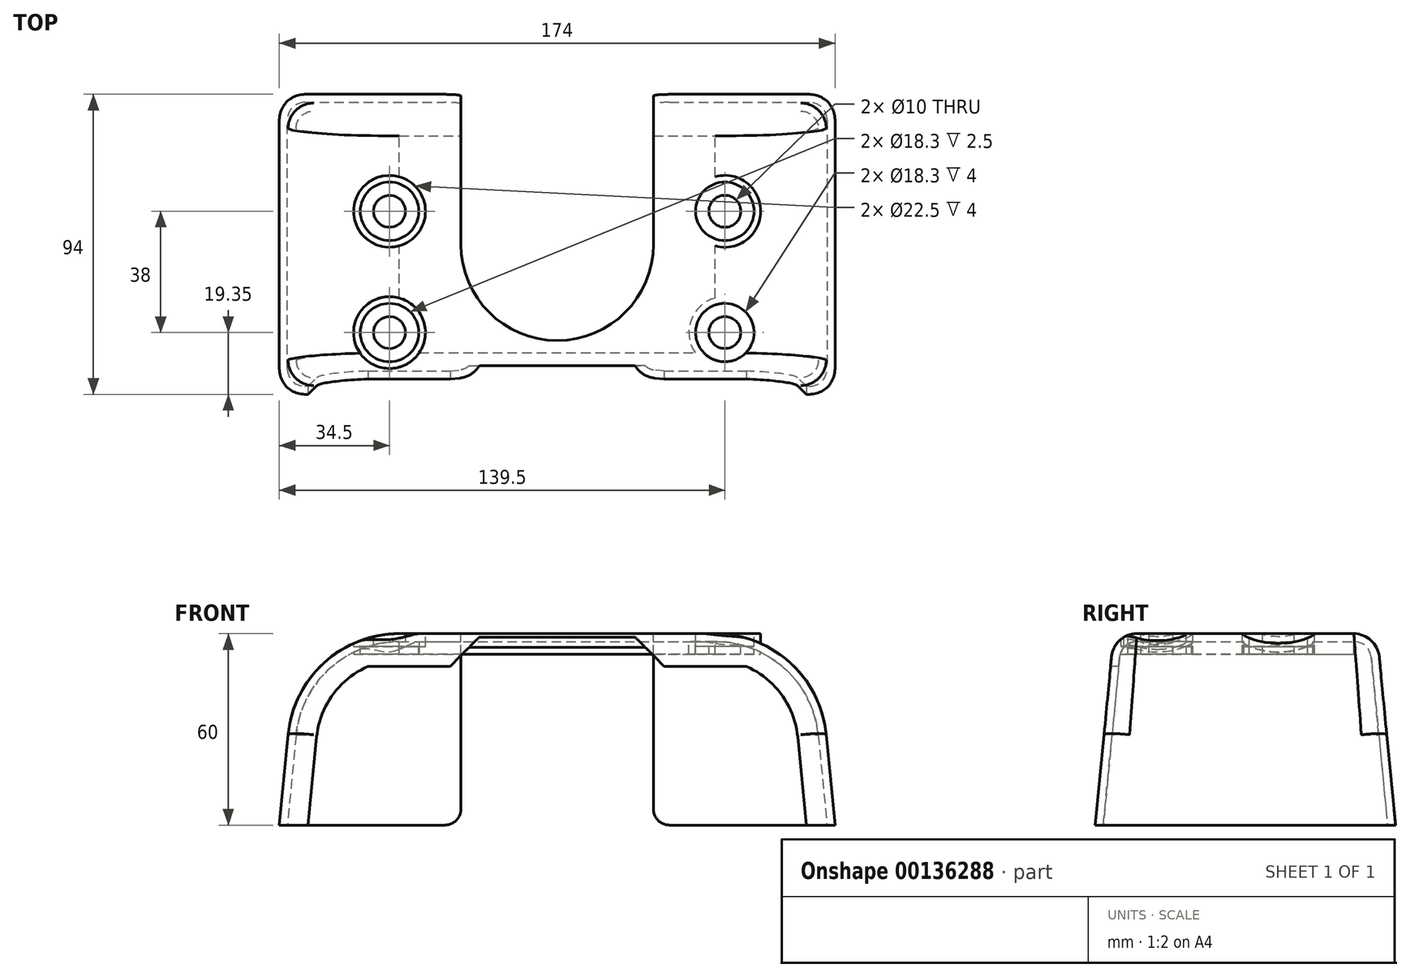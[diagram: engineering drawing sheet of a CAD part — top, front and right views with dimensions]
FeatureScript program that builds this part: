
annotation { "Feature Type Name" : "Feature", "Feature Type Description" : "" }
export const myFeature = defineFeature(function(context is Context, id is Id, definition is map)
    precondition{}
    {
        {
            var Q0;
            Q0=qCreatedBy(makeId("Top.planeOp"),FACE);
            var sketch = newSketch(context, id + "F0", { "sketchPlane" : qUnion([Q0])});
            skLineSegment(sketch, "E0.bottom", {"start": v(-87, -47) * mm, "end": v(87, -47) * mm});
            skLineSegment(sketch, "E0.top", {"start": v(-87, 47) * mm, "end": v(87, 47) * mm});
            skLineSegment(sketch, "E0.left", {"start": v(-87, -47) * mm, "end": v(-87, 47) * mm});
            skLineSegment(sketch, "E0.right", {"start": v(87, -47) * mm, "end": v(87, 47) * mm});
            skPoint(sketch, "E0.middle", {"position": v(0, 0) * mm});
            skSolve(sketch);
        }
        {
            var Q0;
            Q0 = qSketchRegion(id + "F0", true);
            extrude(context, id + "F1", {"entities" : qUnion([Q0]), "depth" : 60 * mm, "hasDraft" : true, "draftAngle" : 5.5 * degree, "draftPullDirection" : true});
        }
        {
            var Q0;
            Q0=makeQuery(id+"F1.opExtrude","CAP_EDGE",EDGE,{"disambiguationData":[OSD([sQuery(id+"F0.wireOp",EDGE,"E0.left")])],"isStart":false});
            var Q1;
            Q1=makeQuery(id+"F1.opExtrude","CAP_EDGE",EDGE,{"disambiguationData":[OSD([sQuery(id+"F0.wireOp",EDGE,"E0.right")])],"isStart":false});
            fillet(context, id + "F2", {"entities" : qUnion([Q0, Q1]), "radius" : 35 * mm, "tangentPropagation" : true, "allowEdgeOverflow" : false});
        }
        {
            var Q0;
            Q0=makeQuery(id+"F1.opExtrude","SWEPT_EDGE",EDGE,{"disambiguationData":[OSD([sQuery(id+"F0.wireOp",EDGE,"E0.bottom"),sQuery(id+"F0.wireOp",EDGE,"E0.left")])]});
            var Q1;
            Q1=makeQuery(id+"F2.opFillet","BLEND_EDGE",EDGE,{"blendedFrom":[makeQuery(id+"F1.opExtrude","CAP_EDGE",EDGE,{"disambiguationData":[OSD([sQuery(id+"F0.wireOp",EDGE,"E0.left")])],"isStart":false}),makeQuery(id+"F1.opExtrude","SWEPT_FACE",FACE,{"disambiguationData":[OSD([sQuery(id+"F0.wireOp",EDGE,"E0.bottom")])]})],"blendedInto":[makeQuery(id+"F1.opExtrude","SWEPT_FACE",FACE,{"disambiguationData":[OSD([sQuery(id+"F0.wireOp",EDGE,"E0.bottom")])]})]});
            var Q2;
            Q2=makeQuery(id+"F1.opExtrude","SWEPT_EDGE",EDGE,{"disambiguationData":[OSD([sQuery(id+"F0.wireOp",EDGE,"E0.top"),sQuery(id+"F0.wireOp",EDGE,"E0.left")])]});
            fillet(context, id + "F3", {"entities" : qUnion([Q0, Q1, Q2]), "radius" : 8 * mm, "tangentPropagation" : true, "allowEdgeOverflow" : false});
        }
        {
            var Q0;
            Q0=makeQuery(id+"F1.opExtrude","CAP_FACE",FACE,{"disambiguationData":[OSD([sQuery(id+"F0.wireOp",EDGE,"E0.bottom"),sQuery(id+"F0.wireOp",EDGE,"E0.top"),sQuery(id+"F0.wireOp",EDGE,"E0.left"),sQuery(id+"F0.wireOp",EDGE,"E0.right")])],"isStart":true});
            shell(context, id + "F4", {"entities" : qUnion([Q0]), "thickness" : 2.5 * mm});
        }
        {
            var Q0;
            Q0=makeQuery(id+"F1.opExtrude","SWEPT_FACE",FACE,{"disambiguationData":[OSD([sQuery(id+"F0.wireOp",EDGE,"E0.bottom")])]});
            var sketch = newSketch(context, id + "F5", { "sketchPlane" : qUnion([Q0])});
            skLineSegment(sketch, "E1", {"start": v(-79.04, -4.5) * mm, "end": v(-73.96, 48.5) * mm});
            skLineSegment(sketch, "E2", {"start": v(79.04, -4.5) * mm, "end": v(73.96, 48.5) * mm});
            skPoint(sketch, "E3.orphan", {"position": v(76.3, 48.5) * mm});
            skLineSegment(sketch, "E4", {"start": v(0, -4.5) * mm, "end": v(0, 43) * mm, "construction": true});
            skPoint(sketch, "E4.endSnap0", {"position": v(0, 48.5) * mm});
            skSolve(sketch);
        }
        {
            var Q0;
            Q0=makeQuery(id+"F1.opExtrude","CAP_FACE",FACE,{"disambiguationData":[OSD([sQuery(id+"F0.wireOp",EDGE,"E0.bottom"),sQuery(id+"F0.wireOp",EDGE,"E0.top"),sQuery(id+"F0.wireOp",EDGE,"E0.left"),sQuery(id+"F0.wireOp",EDGE,"E0.right")])],"isStart":false});
            var sketch = newSketch(context, id + "F6", { "sketchPlane" : qUnion([Q0])});
            skArc(sketch, "E5", {"start": v(-30.15, 0) * mm, "mid": v(0, -30.15) * mm, "end": v(30.15, 0) * mm});
            skLineSegment(sketch, "E6.top", {"start": v(-30.15, 60.3) * mm, "end": v(30.15, 60.3) * mm});
            skLineSegment(sketch, "E6.left", {"start": v(-30.15, 0) * mm, "end": v(-30.15, 60.3) * mm});
            skLineSegment(sketch, "E6.right", {"start": v(30.15, 0) * mm, "end": v(30.15, 60.3) * mm});
            skCircle(sketch, "E7", {"center": v(-52.5, -27.65) * mm, "radius": 11.25 * mm});
            skCircle(sketch, "E8.MirrorC", {"center": v(52.5, -27.65) * mm, "radius": 11.25 * mm});
            skCircle(sketch, "E9.MirrorC", {"center": v(-52.5, 10.35) * mm, "radius": 11.25 * mm});
            skLineSegment(sketch, "E10", {"start": v(-52.3, -38.9) * mm, "end": v(52.5, -38.9) * mm, "construction": true});
            skLineSegment(sketch, "E11", {"start": v(-52.5, -27.65) * mm, "end": v(52.5, -27.65) * mm, "construction": true});
            skPoint(sketch, "E12", {"position": v(0, -30.15) * mm});
            skLineSegment(sketch, "E13", {"start": v(-52.5, 10.35) * mm, "end": v(52.5, 10.35) * mm, "construction": true});
            skCircle(sketch, "E14.MirrorC", {"center": v(52.5, 10.35) * mm, "radius": 11.25 * mm});
            skCircle(sketch, "E15", {"center": v(52.5, -27.65) * mm, "radius": 9.15 * mm});
            skCircle(sketch, "E16.MirrorC", {"center": v(-52.5, -27.65) * mm, "radius": 9.15 * mm});
            skCircle(sketch, "E17", {"center": v(52.5, 10.35) * mm, "radius": 9.15 * mm});
            skCircle(sketch, "E18.MirrorC", {"center": v(-52.5, 10.35) * mm, "radius": 9.15 * mm});
            skCircle(sketch, "E19", {"center": v(52.5, -27.65) * mm, "radius": 5 * mm});
            skCircle(sketch, "E20", {"center": v(52.5, 10.35) * mm, "radius": 5 * mm});
            skCircle(sketch, "E21.MirrorC", {"center": v(-52.5, -27.65) * mm, "radius": 5 * mm});
            skCircle(sketch, "E22.MirrorC", {"center": v(-52.5, 10.35) * mm, "radius": 5 * mm});
            skSolve(sketch);
        }
        {
            var Q0;
            {var subQ0=sQuery(id+"F6.wireOp",EDGE,"E6.top");Q0=makeQuery(id+"F6.imprint","IMPRINT",FACE,{"disambiguationData":[TD([[makeQuery(id+"F6.imprint","IMPRINT",EDGE,{"derivedFrom":subQ0}),-1.0]])]});}
            var Q1;
            {var subQ0=sQuery(id+"F6.wireOp",EDGE,"E5");Q1=makeQuery(id+"F6.imprint","IMPRINT",FACE,{"disambiguationData":[TD([[makeQuery(id+"F6.imprint","IMPRINT",EDGE,{"derivedFrom":subQ0}),1.0]])]});}
            extrude(context, id + "F7", {"entities" : qUnion([Q0, Q1]), "operationType" : NewBodyOperationType.REMOVE, "endBound" : BoundingType.THROUGH_ALL, "oppositeDirection" : true, "depth" : 25 * mm});
        }
        {
            var Q0;
            Q0=makeQuery(id+"F7.boolean.opBoolean","INTERSECT",EDGE,{"derivedFrom":[makeQuery(id+"F1.opExtrude","CAP_FACE",FACE,{"disambiguationData":[OSD([sQuery(id+"F0.wireOp",EDGE,"E0.bottom"),sQuery(id+"F0.wireOp",EDGE,"E0.top"),sQuery(id+"F0.wireOp",EDGE,"E0.left"),sQuery(id+"F0.wireOp",EDGE,"E0.right")])],"isStart":true}),makeQuery(id+"F7.opExtrude","SWEPT_FACE",FACE,{"disambiguationData":[OSD([sQuery(id+"F6.wireOp",EDGE,"E6.left")])]})]});
            var Q1;
            Q1=makeQuery(id+"F7.boolean.opBoolean","INTERSECT",EDGE,{"derivedFrom":[makeQuery(id+"F1.opExtrude","CAP_FACE",FACE,{"disambiguationData":[OSD([sQuery(id+"F0.wireOp",EDGE,"E0.bottom"),sQuery(id+"F0.wireOp",EDGE,"E0.top"),sQuery(id+"F0.wireOp",EDGE,"E0.left"),sQuery(id+"F0.wireOp",EDGE,"E0.right")])],"isStart":true}),makeQuery(id+"F7.opExtrude","SWEPT_FACE",FACE,{"disambiguationData":[OSD([sQuery(id+"F6.wireOp",EDGE,"E6.right")])]})]});
            fillet(context, id + "F8", {"entities" : qUnion([Q0, Q1]), "radius" : 5 * mm, "tangentPropagation" : true, "allowEdgeOverflow" : false});
        }
        {
            var Q0;
            {var subQ0=sQuery(id+"F6.wireOp",EDGE,"E16.MirrorC");var subQ1=sQuery(id+"F0.wireOp",EDGE,"E0.left");var subQ2=sQuery(id+"F0.wireOp",EDGE,"E0.bottom");var subQ3=makeQuery(id+"F1.opExtrude","CAP_FACE",FACE,{"disambiguationData":[OSD([subQ2,sQuery(id+"F0.wireOp",EDGE,"E0.top"),subQ1,sQuery(id+"F0.wireOp",EDGE,"E0.right")])],"isStart":false});var subQ4=makeQuery(id+"F3.opFillet","BLEND_EDGE",EDGE,{"blendedFrom":[makeQuery(id+"F1.opExtrude","CAP_EDGE",EDGE,{"disambiguationData":[OSD([subQ2])],"isStart":false}),subQ3],"blendedInto":[subQ3]});var subQ5=makeQuery(id+"F6.imprint","INTERSECT",VERTEX,{"derivedFrom":[subQ4,subQ0]});Q0=makeQuery(id+"F6.imprint","IMPRINT",FACE,{"disambiguationData":[TD([[makeQuery(id+"F6.imprint","IMPRINT",EDGE,{"disambiguationData":[TD([[subQ5,-1.0]])],"derivedFrom":subQ0}),-1.0]])]});}
            var Q1;
            {var subQ0=sQuery(id+"F6.wireOp",EDGE,"E7");var subQ1=sQuery(id+"F0.wireOp",EDGE,"E0.left");var subQ2=sQuery(id+"F0.wireOp",EDGE,"E0.bottom");var subQ3=makeQuery(id+"F1.opExtrude","CAP_FACE",FACE,{"disambiguationData":[OSD([subQ2,sQuery(id+"F0.wireOp",EDGE,"E0.top"),subQ1,sQuery(id+"F0.wireOp",EDGE,"E0.right")])],"isStart":false});var subQ4=makeQuery(id+"F3.opFillet","BLEND_EDGE",EDGE,{"blendedFrom":[makeQuery(id+"F1.opExtrude","CAP_EDGE",EDGE,{"disambiguationData":[OSD([subQ2])],"isStart":false}),subQ3],"blendedInto":[subQ3]});var subQ5=makeQuery(id+"F6.imprint","INTERSECT",VERTEX,{"derivedFrom":[subQ4,subQ0]});Q1=makeQuery(id+"F6.imprint","IMPRINT",FACE,{"disambiguationData":[TD([[makeQuery(id+"F6.imprint","IMPRINT",EDGE,{"disambiguationData":[TD([[subQ5,1.0]])],"derivedFrom":subQ0}),1.0]])]});}
            var Q2;
            {var subQ0=sQuery(id+"F6.wireOp",EDGE,"E16.MirrorC");var subQ1=sQuery(id+"F0.wireOp",EDGE,"E0.left");var subQ2=sQuery(id+"F0.wireOp",EDGE,"E0.bottom");var subQ3=makeQuery(id+"F1.opExtrude","CAP_FACE",FACE,{"disambiguationData":[OSD([subQ2,sQuery(id+"F0.wireOp",EDGE,"E0.top"),subQ1,sQuery(id+"F0.wireOp",EDGE,"E0.right")])],"isStart":false});var subQ4=makeQuery(id+"F3.opFillet","BLEND_EDGE",EDGE,{"blendedFrom":[makeQuery(id+"F1.opExtrude","CAP_EDGE",EDGE,{"disambiguationData":[OSD([subQ2])],"isStart":false}),subQ3],"blendedInto":[subQ3]});var subQ5=makeQuery(id+"F6.imprint","INTERSECT",VERTEX,{"derivedFrom":[subQ4,subQ0]});Q2=makeQuery(id+"F6.imprint","IMPRINT",FACE,{"disambiguationData":[TD([[makeQuery(id+"F6.imprint","IMPRINT",EDGE,{"disambiguationData":[TD([[subQ5,1.0]])],"derivedFrom":subQ0}),-1.0]])]});}
            var Q3;
            {var subQ0=sQuery(id+"F6.wireOp",EDGE,"E7");var subQ1=sQuery(id+"F0.wireOp",EDGE,"E0.left");var subQ2=sQuery(id+"F0.wireOp",EDGE,"E0.bottom");var subQ3=makeQuery(id+"F1.opExtrude","CAP_FACE",FACE,{"disambiguationData":[OSD([subQ2,sQuery(id+"F0.wireOp",EDGE,"E0.top"),subQ1,sQuery(id+"F0.wireOp",EDGE,"E0.right")])],"isStart":false});var subQ4=makeQuery(id+"F3.opFillet","BLEND_EDGE",EDGE,{"blendedFrom":[makeQuery(id+"F1.opExtrude","CAP_EDGE",EDGE,{"disambiguationData":[OSD([subQ2])],"isStart":false}),subQ3],"blendedInto":[subQ3]});var subQ5=makeQuery(id+"F6.imprint","INTERSECT",VERTEX,{"derivedFrom":[subQ4,subQ0]});Q3=makeQuery(id+"F6.imprint","IMPRINT",FACE,{"disambiguationData":[TD([[makeQuery(id+"F6.imprint","IMPRINT",EDGE,{"disambiguationData":[TD([[subQ5,-1.0]])],"derivedFrom":subQ0}),1.0]])]});}
            var Q4;
            {var subQ0=sQuery(id+"F6.wireOp",EDGE,"E9.MirrorC");var subQ1=sQuery(id+"F0.wireOp",EDGE,"E0.left");var subQ2=makeQuery(id+"F2.opFillet","BLEND_EDGE",EDGE,{"blendedFrom":[makeQuery(id+"F1.opExtrude","CAP_EDGE",EDGE,{"disambiguationData":[OSD([subQ1])],"isStart":false}),makeQuery(id+"F1.opExtrude","CAP_FACE",FACE,{"disambiguationData":[OSD([sQuery(id+"F0.wireOp",EDGE,"E0.bottom"),sQuery(id+"F0.wireOp",EDGE,"E0.top"),subQ1,sQuery(id+"F0.wireOp",EDGE,"E0.right")])],"isStart":false})],"blendedInto":[makeQuery(id+"F1.opExtrude","CAP_FACE",FACE,{"disambiguationData":[OSD([sQuery(id+"F0.wireOp",EDGE,"E0.bottom"),sQuery(id+"F0.wireOp",EDGE,"E0.top"),subQ1,sQuery(id+"F0.wireOp",EDGE,"E0.right")])],"isStart":false})]});var subQ3=makeQuery(id+"F6.imprint","INTERSECT",VERTEX,{"disambiguationData":[OD(0.0)],"derivedFrom":[subQ2,subQ0]});Q4=makeQuery(id+"F6.imprint","IMPRINT",FACE,{"disambiguationData":[TD([[makeQuery(id+"F6.imprint","IMPRINT",EDGE,{"disambiguationData":[TD([[subQ3,1.0]])],"derivedFrom":subQ0}),-1.0]])]});}
            var Q5;
            {var subQ0=sQuery(id+"F6.wireOp",EDGE,"E18.MirrorC");var subQ1=sQuery(id+"F0.wireOp",EDGE,"E0.left");var subQ2=makeQuery(id+"F2.opFillet","BLEND_EDGE",EDGE,{"blendedFrom":[makeQuery(id+"F1.opExtrude","CAP_EDGE",EDGE,{"disambiguationData":[OSD([subQ1])],"isStart":false}),makeQuery(id+"F1.opExtrude","CAP_FACE",FACE,{"disambiguationData":[OSD([sQuery(id+"F0.wireOp",EDGE,"E0.bottom"),sQuery(id+"F0.wireOp",EDGE,"E0.top"),subQ1,sQuery(id+"F0.wireOp",EDGE,"E0.right")])],"isStart":false})],"blendedInto":[makeQuery(id+"F1.opExtrude","CAP_FACE",FACE,{"disambiguationData":[OSD([sQuery(id+"F0.wireOp",EDGE,"E0.bottom"),sQuery(id+"F0.wireOp",EDGE,"E0.top"),subQ1,sQuery(id+"F0.wireOp",EDGE,"E0.right")])],"isStart":false})]});var subQ3=makeQuery(id+"F6.imprint","INTERSECT",VERTEX,{"disambiguationData":[OD(0.0)],"derivedFrom":[subQ2,subQ0]});Q5=makeQuery(id+"F6.imprint","IMPRINT",FACE,{"disambiguationData":[TD([[makeQuery(id+"F6.imprint","IMPRINT",EDGE,{"disambiguationData":[TD([[subQ3,1.0]])],"derivedFrom":subQ0}),-1.0]])]});}
            var Q6;
            {var subQ0=sQuery(id+"F6.wireOp",EDGE,"E9.MirrorC");var subQ1=sQuery(id+"F0.wireOp",EDGE,"E0.left");var subQ2=makeQuery(id+"F2.opFillet","BLEND_EDGE",EDGE,{"blendedFrom":[makeQuery(id+"F1.opExtrude","CAP_EDGE",EDGE,{"disambiguationData":[OSD([subQ1])],"isStart":false}),makeQuery(id+"F1.opExtrude","CAP_FACE",FACE,{"disambiguationData":[OSD([sQuery(id+"F0.wireOp",EDGE,"E0.bottom"),sQuery(id+"F0.wireOp",EDGE,"E0.top"),subQ1,sQuery(id+"F0.wireOp",EDGE,"E0.right")])],"isStart":false})],"blendedInto":[makeQuery(id+"F1.opExtrude","CAP_FACE",FACE,{"disambiguationData":[OSD([sQuery(id+"F0.wireOp",EDGE,"E0.bottom"),sQuery(id+"F0.wireOp",EDGE,"E0.top"),subQ1,sQuery(id+"F0.wireOp",EDGE,"E0.right")])],"isStart":false})]});var subQ3=makeQuery(id+"F6.imprint","INTERSECT",VERTEX,{"disambiguationData":[OD(0.0)],"derivedFrom":[subQ2,subQ0]});Q6=makeQuery(id+"F6.imprint","IMPRINT",FACE,{"disambiguationData":[TD([[makeQuery(id+"F6.imprint","IMPRINT",EDGE,{"disambiguationData":[TD([[subQ3,-1.0]])],"derivedFrom":subQ0}),-1.0]])]});}
            var Q7;
            {var subQ0=sQuery(id+"F6.wireOp",EDGE,"E18.MirrorC");var subQ1=sQuery(id+"F0.wireOp",EDGE,"E0.left");var subQ2=makeQuery(id+"F2.opFillet","BLEND_EDGE",EDGE,{"blendedFrom":[makeQuery(id+"F1.opExtrude","CAP_EDGE",EDGE,{"disambiguationData":[OSD([subQ1])],"isStart":false}),makeQuery(id+"F1.opExtrude","CAP_FACE",FACE,{"disambiguationData":[OSD([sQuery(id+"F0.wireOp",EDGE,"E0.bottom"),sQuery(id+"F0.wireOp",EDGE,"E0.top"),subQ1,sQuery(id+"F0.wireOp",EDGE,"E0.right")])],"isStart":false})],"blendedInto":[makeQuery(id+"F1.opExtrude","CAP_FACE",FACE,{"disambiguationData":[OSD([sQuery(id+"F0.wireOp",EDGE,"E0.bottom"),sQuery(id+"F0.wireOp",EDGE,"E0.top"),subQ1,sQuery(id+"F0.wireOp",EDGE,"E0.right")])],"isStart":false})]});var subQ3=makeQuery(id+"F6.imprint","INTERSECT",VERTEX,{"disambiguationData":[OD(0.0)],"derivedFrom":[subQ2,subQ0]});Q7=makeQuery(id+"F6.imprint","IMPRINT",FACE,{"disambiguationData":[TD([[makeQuery(id+"F6.imprint","IMPRINT",EDGE,{"disambiguationData":[TD([[subQ3,-1.0]])],"derivedFrom":subQ0}),-1.0]])]});}
            var Q8;
            {var subQ0=sQuery(id+"F6.wireOp",EDGE,"E15");var subQ1=sQuery(id+"F0.wireOp",EDGE,"E0.right");var subQ2=sQuery(id+"F0.wireOp",EDGE,"E0.bottom");var subQ3=makeQuery(id+"F1.opExtrude","CAP_FACE",FACE,{"disambiguationData":[OSD([subQ2,sQuery(id+"F0.wireOp",EDGE,"E0.top"),sQuery(id+"F0.wireOp",EDGE,"E0.left"),subQ1])],"isStart":false});var subQ4=makeQuery(id+"F3.opFillet","BLEND_EDGE",EDGE,{"blendedFrom":[makeQuery(id+"F1.opExtrude","CAP_EDGE",EDGE,{"disambiguationData":[OSD([subQ2])],"isStart":false}),subQ3],"blendedInto":[subQ3]});var subQ5=makeQuery(id+"F6.imprint","INTERSECT",VERTEX,{"derivedFrom":[subQ4,subQ0]});Q8=makeQuery(id+"F6.imprint","IMPRINT",FACE,{"disambiguationData":[TD([[makeQuery(id+"F6.imprint","IMPRINT",EDGE,{"disambiguationData":[TD([[subQ5,-1.0]])],"derivedFrom":subQ0}),1.0]])]});}
            var Q9;
            {var subQ0=sQuery(id+"F6.wireOp",EDGE,"E8.MirrorC");var subQ1=sQuery(id+"F0.wireOp",EDGE,"E0.right");var subQ2=sQuery(id+"F0.wireOp",EDGE,"E0.bottom");var subQ3=makeQuery(id+"F1.opExtrude","CAP_FACE",FACE,{"disambiguationData":[OSD([subQ2,sQuery(id+"F0.wireOp",EDGE,"E0.top"),sQuery(id+"F0.wireOp",EDGE,"E0.left"),subQ1])],"isStart":false});var subQ4=makeQuery(id+"F3.opFillet","BLEND_EDGE",EDGE,{"blendedFrom":[makeQuery(id+"F1.opExtrude","CAP_EDGE",EDGE,{"disambiguationData":[OSD([subQ2])],"isStart":false}),subQ3],"blendedInto":[subQ3]});var subQ5=makeQuery(id+"F6.imprint","INTERSECT",VERTEX,{"derivedFrom":[subQ4,subQ0]});Q9=makeQuery(id+"F6.imprint","IMPRINT",FACE,{"disambiguationData":[TD([[makeQuery(id+"F6.imprint","IMPRINT",EDGE,{"disambiguationData":[TD([[subQ5,1.0]])],"derivedFrom":subQ0}),-1.0]])]});}
            var Q10;
            {var subQ0=sQuery(id+"F6.wireOp",EDGE,"E15");var subQ1=sQuery(id+"F0.wireOp",EDGE,"E0.right");var subQ2=sQuery(id+"F0.wireOp",EDGE,"E0.bottom");var subQ3=makeQuery(id+"F1.opExtrude","CAP_FACE",FACE,{"disambiguationData":[OSD([subQ2,sQuery(id+"F0.wireOp",EDGE,"E0.top"),sQuery(id+"F0.wireOp",EDGE,"E0.left"),subQ1])],"isStart":false});var subQ4=makeQuery(id+"F3.opFillet","BLEND_EDGE",EDGE,{"blendedFrom":[makeQuery(id+"F1.opExtrude","CAP_EDGE",EDGE,{"disambiguationData":[OSD([subQ2])],"isStart":false}),subQ3],"blendedInto":[subQ3]});var subQ5=makeQuery(id+"F6.imprint","INTERSECT",VERTEX,{"derivedFrom":[subQ4,subQ0]});Q10=makeQuery(id+"F6.imprint","IMPRINT",FACE,{"disambiguationData":[TD([[makeQuery(id+"F6.imprint","IMPRINT",EDGE,{"disambiguationData":[TD([[subQ5,1.0]])],"derivedFrom":subQ0}),1.0]])]});}
            var Q11;
            {var subQ0=sQuery(id+"F6.wireOp",EDGE,"E8.MirrorC");var subQ1=sQuery(id+"F0.wireOp",EDGE,"E0.right");var subQ2=sQuery(id+"F0.wireOp",EDGE,"E0.bottom");var subQ3=makeQuery(id+"F1.opExtrude","CAP_FACE",FACE,{"disambiguationData":[OSD([subQ2,sQuery(id+"F0.wireOp",EDGE,"E0.top"),sQuery(id+"F0.wireOp",EDGE,"E0.left"),subQ1])],"isStart":false});var subQ4=makeQuery(id+"F3.opFillet","BLEND_EDGE",EDGE,{"blendedFrom":[makeQuery(id+"F1.opExtrude","CAP_EDGE",EDGE,{"disambiguationData":[OSD([subQ2])],"isStart":false}),subQ3],"blendedInto":[subQ3]});var subQ5=makeQuery(id+"F6.imprint","INTERSECT",VERTEX,{"derivedFrom":[subQ4,subQ0]});Q11=makeQuery(id+"F6.imprint","IMPRINT",FACE,{"disambiguationData":[TD([[makeQuery(id+"F6.imprint","IMPRINT",EDGE,{"disambiguationData":[TD([[subQ5,-1.0]])],"derivedFrom":subQ0}),-1.0]])]});}
            var Q12;
            {var subQ0=sQuery(id+"F6.wireOp",EDGE,"E14.MirrorC");var subQ1=sQuery(id+"F0.wireOp",EDGE,"E0.right");var subQ2=makeQuery(id+"F2.opFillet","BLEND_EDGE",EDGE,{"blendedFrom":[makeQuery(id+"F1.opExtrude","CAP_EDGE",EDGE,{"disambiguationData":[OSD([subQ1])],"isStart":false}),makeQuery(id+"F1.opExtrude","CAP_FACE",FACE,{"disambiguationData":[OSD([sQuery(id+"F0.wireOp",EDGE,"E0.bottom"),sQuery(id+"F0.wireOp",EDGE,"E0.top"),sQuery(id+"F0.wireOp",EDGE,"E0.left"),subQ1])],"isStart":false})],"blendedInto":[makeQuery(id+"F1.opExtrude","CAP_FACE",FACE,{"disambiguationData":[OSD([sQuery(id+"F0.wireOp",EDGE,"E0.bottom"),sQuery(id+"F0.wireOp",EDGE,"E0.top"),sQuery(id+"F0.wireOp",EDGE,"E0.left"),subQ1])],"isStart":false})]});var subQ3=makeQuery(id+"F6.imprint","INTERSECT",VERTEX,{"disambiguationData":[OD(0.0)],"derivedFrom":[subQ2,subQ0]});Q12=makeQuery(id+"F6.imprint","IMPRINT",FACE,{"disambiguationData":[TD([[makeQuery(id+"F6.imprint","IMPRINT",EDGE,{"disambiguationData":[TD([[subQ3,-1.0]])],"derivedFrom":subQ0}),1.0]])]});}
            var Q13;
            {var subQ0=sQuery(id+"F6.wireOp",EDGE,"E17");var subQ1=sQuery(id+"F0.wireOp",EDGE,"E0.right");var subQ2=makeQuery(id+"F2.opFillet","BLEND_EDGE",EDGE,{"blendedFrom":[makeQuery(id+"F1.opExtrude","CAP_EDGE",EDGE,{"disambiguationData":[OSD([subQ1])],"isStart":false}),makeQuery(id+"F1.opExtrude","CAP_FACE",FACE,{"disambiguationData":[OSD([sQuery(id+"F0.wireOp",EDGE,"E0.bottom"),sQuery(id+"F0.wireOp",EDGE,"E0.top"),sQuery(id+"F0.wireOp",EDGE,"E0.left"),subQ1])],"isStart":false})],"blendedInto":[makeQuery(id+"F1.opExtrude","CAP_FACE",FACE,{"disambiguationData":[OSD([sQuery(id+"F0.wireOp",EDGE,"E0.bottom"),sQuery(id+"F0.wireOp",EDGE,"E0.top"),sQuery(id+"F0.wireOp",EDGE,"E0.left"),subQ1])],"isStart":false})]});var subQ3=makeQuery(id+"F6.imprint","INTERSECT",VERTEX,{"disambiguationData":[OD(0.0)],"derivedFrom":[subQ2,subQ0]});Q13=makeQuery(id+"F6.imprint","IMPRINT",FACE,{"disambiguationData":[TD([[makeQuery(id+"F6.imprint","IMPRINT",EDGE,{"disambiguationData":[TD([[subQ3,-1.0]])],"derivedFrom":subQ0}),1.0]])]});}
            var Q14;
            {var subQ0=sQuery(id+"F6.wireOp",EDGE,"E17");var subQ1=sQuery(id+"F0.wireOp",EDGE,"E0.right");var subQ2=makeQuery(id+"F2.opFillet","BLEND_EDGE",EDGE,{"blendedFrom":[makeQuery(id+"F1.opExtrude","CAP_EDGE",EDGE,{"disambiguationData":[OSD([subQ1])],"isStart":false}),makeQuery(id+"F1.opExtrude","CAP_FACE",FACE,{"disambiguationData":[OSD([sQuery(id+"F0.wireOp",EDGE,"E0.bottom"),sQuery(id+"F0.wireOp",EDGE,"E0.top"),sQuery(id+"F0.wireOp",EDGE,"E0.left"),subQ1])],"isStart":false})],"blendedInto":[makeQuery(id+"F1.opExtrude","CAP_FACE",FACE,{"disambiguationData":[OSD([sQuery(id+"F0.wireOp",EDGE,"E0.bottom"),sQuery(id+"F0.wireOp",EDGE,"E0.top"),sQuery(id+"F0.wireOp",EDGE,"E0.left"),subQ1])],"isStart":false})]});var subQ3=makeQuery(id+"F6.imprint","INTERSECT",VERTEX,{"disambiguationData":[OD(0.0)],"derivedFrom":[subQ2,subQ0]});Q14=makeQuery(id+"F6.imprint","IMPRINT",FACE,{"disambiguationData":[TD([[makeQuery(id+"F6.imprint","IMPRINT",EDGE,{"disambiguationData":[TD([[subQ3,1.0]])],"derivedFrom":subQ0}),1.0]])]});}
            var Q15;
            {var subQ0=sQuery(id+"F6.wireOp",EDGE,"E14.MirrorC");var subQ1=sQuery(id+"F0.wireOp",EDGE,"E0.right");var subQ2=makeQuery(id+"F2.opFillet","BLEND_EDGE",EDGE,{"blendedFrom":[makeQuery(id+"F1.opExtrude","CAP_EDGE",EDGE,{"disambiguationData":[OSD([subQ1])],"isStart":false}),makeQuery(id+"F1.opExtrude","CAP_FACE",FACE,{"disambiguationData":[OSD([sQuery(id+"F0.wireOp",EDGE,"E0.bottom"),sQuery(id+"F0.wireOp",EDGE,"E0.top"),sQuery(id+"F0.wireOp",EDGE,"E0.left"),subQ1])],"isStart":false})],"blendedInto":[makeQuery(id+"F1.opExtrude","CAP_FACE",FACE,{"disambiguationData":[OSD([sQuery(id+"F0.wireOp",EDGE,"E0.bottom"),sQuery(id+"F0.wireOp",EDGE,"E0.top"),sQuery(id+"F0.wireOp",EDGE,"E0.left"),subQ1])],"isStart":false})]});var subQ3=makeQuery(id+"F6.imprint","INTERSECT",VERTEX,{"disambiguationData":[OD(0.0)],"derivedFrom":[subQ2,subQ0]});Q15=makeQuery(id+"F6.imprint","IMPRINT",FACE,{"disambiguationData":[TD([[makeQuery(id+"F6.imprint","IMPRINT",EDGE,{"disambiguationData":[TD([[subQ3,1.0]])],"derivedFrom":subQ0}),1.0]])]});}
            extrude(context, id + "F9", {"entities" : qUnion([Q0, Q1, Q2, Q3, Q4, Q5, Q6, Q7, Q8, Q9, Q10, Q11, Q12, Q13, Q14, Q15]), "operationType" : NewBodyOperationType.ADD, "oppositeDirection" : true, "depth" : 6.5 * mm});
        }
        {
            var Q0;
            {var subQ0=sQuery(id+"F6.wireOp",EDGE,"E15");var subQ1=sQuery(id+"F0.wireOp",EDGE,"E0.right");var subQ2=sQuery(id+"F0.wireOp",EDGE,"E0.bottom");var subQ3=makeQuery(id+"F1.opExtrude","CAP_FACE",FACE,{"disambiguationData":[OSD([subQ2,sQuery(id+"F0.wireOp",EDGE,"E0.top"),sQuery(id+"F0.wireOp",EDGE,"E0.left"),subQ1])],"isStart":false});var subQ4=makeQuery(id+"F3.opFillet","BLEND_EDGE",EDGE,{"blendedFrom":[makeQuery(id+"F1.opExtrude","CAP_EDGE",EDGE,{"disambiguationData":[OSD([subQ2])],"isStart":false}),subQ3],"blendedInto":[subQ3]});var subQ5=makeQuery(id+"F6.imprint","INTERSECT",VERTEX,{"derivedFrom":[subQ4,subQ0]});Q0=makeQuery(id+"F6.imprint","IMPRINT",FACE,{"disambiguationData":[TD([[makeQuery(id+"F6.imprint","IMPRINT",EDGE,{"disambiguationData":[TD([[subQ5,-1.0]])],"derivedFrom":subQ0}),1.0]])]});}
            var Q1;
            {var subQ0=sQuery(id+"F6.wireOp",EDGE,"E15");var subQ1=sQuery(id+"F0.wireOp",EDGE,"E0.right");var subQ2=sQuery(id+"F0.wireOp",EDGE,"E0.bottom");var subQ3=makeQuery(id+"F1.opExtrude","CAP_FACE",FACE,{"disambiguationData":[OSD([subQ2,sQuery(id+"F0.wireOp",EDGE,"E0.top"),sQuery(id+"F0.wireOp",EDGE,"E0.left"),subQ1])],"isStart":false});var subQ4=makeQuery(id+"F3.opFillet","BLEND_EDGE",EDGE,{"blendedFrom":[makeQuery(id+"F1.opExtrude","CAP_EDGE",EDGE,{"disambiguationData":[OSD([subQ2])],"isStart":false}),subQ3],"blendedInto":[subQ3]});var subQ5=makeQuery(id+"F6.imprint","INTERSECT",VERTEX,{"derivedFrom":[subQ4,subQ0]});Q1=makeQuery(id+"F6.imprint","IMPRINT",FACE,{"disambiguationData":[TD([[makeQuery(id+"F6.imprint","IMPRINT",EDGE,{"disambiguationData":[TD([[subQ5,1.0]])],"derivedFrom":subQ0}),1.0]])]});}
            var Q2;
            {var subQ0=sQuery(id+"F6.wireOp",EDGE,"E17");var subQ1=sQuery(id+"F0.wireOp",EDGE,"E0.right");var subQ2=makeQuery(id+"F2.opFillet","BLEND_EDGE",EDGE,{"blendedFrom":[makeQuery(id+"F1.opExtrude","CAP_EDGE",EDGE,{"disambiguationData":[OSD([subQ1])],"isStart":false}),makeQuery(id+"F1.opExtrude","CAP_FACE",FACE,{"disambiguationData":[OSD([sQuery(id+"F0.wireOp",EDGE,"E0.bottom"),sQuery(id+"F0.wireOp",EDGE,"E0.top"),sQuery(id+"F0.wireOp",EDGE,"E0.left"),subQ1])],"isStart":false})],"blendedInto":[makeQuery(id+"F1.opExtrude","CAP_FACE",FACE,{"disambiguationData":[OSD([sQuery(id+"F0.wireOp",EDGE,"E0.bottom"),sQuery(id+"F0.wireOp",EDGE,"E0.top"),sQuery(id+"F0.wireOp",EDGE,"E0.left"),subQ1])],"isStart":false})]});var subQ3=makeQuery(id+"F6.imprint","INTERSECT",VERTEX,{"disambiguationData":[OD(0.0)],"derivedFrom":[subQ2,subQ0]});Q2=makeQuery(id+"F6.imprint","IMPRINT",FACE,{"disambiguationData":[TD([[makeQuery(id+"F6.imprint","IMPRINT",EDGE,{"disambiguationData":[TD([[subQ3,1.0]])],"derivedFrom":subQ0}),1.0]])]});}
            var Q3;
            {var subQ0=sQuery(id+"F6.wireOp",EDGE,"E17");var subQ1=sQuery(id+"F0.wireOp",EDGE,"E0.right");var subQ2=makeQuery(id+"F2.opFillet","BLEND_EDGE",EDGE,{"blendedFrom":[makeQuery(id+"F1.opExtrude","CAP_EDGE",EDGE,{"disambiguationData":[OSD([subQ1])],"isStart":false}),makeQuery(id+"F1.opExtrude","CAP_FACE",FACE,{"disambiguationData":[OSD([sQuery(id+"F0.wireOp",EDGE,"E0.bottom"),sQuery(id+"F0.wireOp",EDGE,"E0.top"),sQuery(id+"F0.wireOp",EDGE,"E0.left"),subQ1])],"isStart":false})],"blendedInto":[makeQuery(id+"F1.opExtrude","CAP_FACE",FACE,{"disambiguationData":[OSD([sQuery(id+"F0.wireOp",EDGE,"E0.bottom"),sQuery(id+"F0.wireOp",EDGE,"E0.top"),sQuery(id+"F0.wireOp",EDGE,"E0.left"),subQ1])],"isStart":false})]});var subQ3=makeQuery(id+"F6.imprint","INTERSECT",VERTEX,{"disambiguationData":[OD(0.0)],"derivedFrom":[subQ2,subQ0]});Q3=makeQuery(id+"F6.imprint","IMPRINT",FACE,{"disambiguationData":[TD([[makeQuery(id+"F6.imprint","IMPRINT",EDGE,{"disambiguationData":[TD([[subQ3,-1.0]])],"derivedFrom":subQ0}),1.0]])]});}
            var Q4;
            {var subQ0=sQuery(id+"F6.wireOp",EDGE,"E16.MirrorC");var subQ1=sQuery(id+"F0.wireOp",EDGE,"E0.left");var subQ2=sQuery(id+"F0.wireOp",EDGE,"E0.bottom");var subQ3=makeQuery(id+"F1.opExtrude","CAP_FACE",FACE,{"disambiguationData":[OSD([subQ2,sQuery(id+"F0.wireOp",EDGE,"E0.top"),subQ1,sQuery(id+"F0.wireOp",EDGE,"E0.right")])],"isStart":false});var subQ4=makeQuery(id+"F3.opFillet","BLEND_EDGE",EDGE,{"blendedFrom":[makeQuery(id+"F1.opExtrude","CAP_EDGE",EDGE,{"disambiguationData":[OSD([subQ2])],"isStart":false}),subQ3],"blendedInto":[subQ3]});var subQ5=makeQuery(id+"F6.imprint","INTERSECT",VERTEX,{"derivedFrom":[subQ4,subQ0]});Q4=makeQuery(id+"F6.imprint","IMPRINT",FACE,{"disambiguationData":[TD([[makeQuery(id+"F6.imprint","IMPRINT",EDGE,{"disambiguationData":[TD([[subQ5,1.0]])],"derivedFrom":subQ0}),-1.0]])]});}
            var Q5;
            {var subQ0=sQuery(id+"F6.wireOp",EDGE,"E16.MirrorC");var subQ1=sQuery(id+"F0.wireOp",EDGE,"E0.left");var subQ2=sQuery(id+"F0.wireOp",EDGE,"E0.bottom");var subQ3=makeQuery(id+"F1.opExtrude","CAP_FACE",FACE,{"disambiguationData":[OSD([subQ2,sQuery(id+"F0.wireOp",EDGE,"E0.top"),subQ1,sQuery(id+"F0.wireOp",EDGE,"E0.right")])],"isStart":false});var subQ4=makeQuery(id+"F3.opFillet","BLEND_EDGE",EDGE,{"blendedFrom":[makeQuery(id+"F1.opExtrude","CAP_EDGE",EDGE,{"disambiguationData":[OSD([subQ2])],"isStart":false}),subQ3],"blendedInto":[subQ3]});var subQ5=makeQuery(id+"F6.imprint","INTERSECT",VERTEX,{"derivedFrom":[subQ4,subQ0]});Q5=makeQuery(id+"F6.imprint","IMPRINT",FACE,{"disambiguationData":[TD([[makeQuery(id+"F6.imprint","IMPRINT",EDGE,{"disambiguationData":[TD([[subQ5,-1.0]])],"derivedFrom":subQ0}),-1.0]])]});}
            var Q6;
            {var subQ0=sQuery(id+"F6.wireOp",EDGE,"E18.MirrorC");var subQ1=sQuery(id+"F0.wireOp",EDGE,"E0.left");var subQ2=makeQuery(id+"F2.opFillet","BLEND_EDGE",EDGE,{"blendedFrom":[makeQuery(id+"F1.opExtrude","CAP_EDGE",EDGE,{"disambiguationData":[OSD([subQ1])],"isStart":false}),makeQuery(id+"F1.opExtrude","CAP_FACE",FACE,{"disambiguationData":[OSD([sQuery(id+"F0.wireOp",EDGE,"E0.bottom"),sQuery(id+"F0.wireOp",EDGE,"E0.top"),subQ1,sQuery(id+"F0.wireOp",EDGE,"E0.right")])],"isStart":false})],"blendedInto":[makeQuery(id+"F1.opExtrude","CAP_FACE",FACE,{"disambiguationData":[OSD([sQuery(id+"F0.wireOp",EDGE,"E0.bottom"),sQuery(id+"F0.wireOp",EDGE,"E0.top"),subQ1,sQuery(id+"F0.wireOp",EDGE,"E0.right")])],"isStart":false})]});var subQ3=makeQuery(id+"F6.imprint","INTERSECT",VERTEX,{"disambiguationData":[OD(0.0)],"derivedFrom":[subQ2,subQ0]});Q6=makeQuery(id+"F6.imprint","IMPRINT",FACE,{"disambiguationData":[TD([[makeQuery(id+"F6.imprint","IMPRINT",EDGE,{"disambiguationData":[TD([[subQ3,1.0]])],"derivedFrom":subQ0}),-1.0]])]});}
            var Q7;
            {var subQ0=sQuery(id+"F6.wireOp",EDGE,"E18.MirrorC");var subQ1=sQuery(id+"F0.wireOp",EDGE,"E0.left");var subQ2=makeQuery(id+"F2.opFillet","BLEND_EDGE",EDGE,{"blendedFrom":[makeQuery(id+"F1.opExtrude","CAP_EDGE",EDGE,{"disambiguationData":[OSD([subQ1])],"isStart":false}),makeQuery(id+"F1.opExtrude","CAP_FACE",FACE,{"disambiguationData":[OSD([sQuery(id+"F0.wireOp",EDGE,"E0.bottom"),sQuery(id+"F0.wireOp",EDGE,"E0.top"),subQ1,sQuery(id+"F0.wireOp",EDGE,"E0.right")])],"isStart":false})],"blendedInto":[makeQuery(id+"F1.opExtrude","CAP_FACE",FACE,{"disambiguationData":[OSD([sQuery(id+"F0.wireOp",EDGE,"E0.bottom"),sQuery(id+"F0.wireOp",EDGE,"E0.top"),subQ1,sQuery(id+"F0.wireOp",EDGE,"E0.right")])],"isStart":false})]});var subQ3=makeQuery(id+"F6.imprint","INTERSECT",VERTEX,{"disambiguationData":[OD(0.0)],"derivedFrom":[subQ2,subQ0]});Q7=makeQuery(id+"F6.imprint","IMPRINT",FACE,{"disambiguationData":[TD([[makeQuery(id+"F6.imprint","IMPRINT",EDGE,{"disambiguationData":[TD([[subQ3,-1.0]])],"derivedFrom":subQ0}),-1.0]])]});}
            var Q8;
            Q8=sQuery(id+"F6.wireOp",EDGE,"E15");
            var Q9;
            Q9=sQuery(id+"F6.wireOp",EDGE,"E17");
            var Q10;
            Q10=sQuery(id+"F6.wireOp",EDGE,"E18.MirrorC");
            var Q11;
            Q11=sQuery(id+"F6.wireOp",EDGE,"E16.MirrorC");
            extrude(context, id + "F10", {"entities" : qUnion([Q0, Q1, Q2, Q3, Q4, Q5, Q6, Q7]), "operationType" : NewBodyOperationType.REMOVE, "surfaceEntities" : qUnion([Q8, Q9, Q10, Q11]), "oppositeDirection" : true, "depth" : 4 * mm});
        }
        {
            var Q0;
            {var subQ0=sQuery(id+"F6.wireOp",EDGE,"E19");var subQ1=sQuery(id+"F0.wireOp",EDGE,"E0.right");var subQ2=makeQuery(id+"F2.opFillet","BLEND_EDGE",EDGE,{"blendedFrom":[makeQuery(id+"F1.opExtrude","CAP_EDGE",EDGE,{"disambiguationData":[OSD([subQ1])],"isStart":false}),makeQuery(id+"F1.opExtrude","CAP_FACE",FACE,{"disambiguationData":[OSD([sQuery(id+"F0.wireOp",EDGE,"E0.bottom"),sQuery(id+"F0.wireOp",EDGE,"E0.top"),sQuery(id+"F0.wireOp",EDGE,"E0.left"),subQ1])],"isStart":false})],"blendedInto":[makeQuery(id+"F1.opExtrude","CAP_FACE",FACE,{"disambiguationData":[OSD([sQuery(id+"F0.wireOp",EDGE,"E0.bottom"),sQuery(id+"F0.wireOp",EDGE,"E0.top"),sQuery(id+"F0.wireOp",EDGE,"E0.left"),subQ1])],"isStart":false})]});var subQ3=makeQuery(id+"F6.imprint","INTERSECT",VERTEX,{"disambiguationData":[OD(0.0)],"derivedFrom":[subQ2,subQ0]});Q0=makeQuery(id+"F6.imprint","IMPRINT",FACE,{"disambiguationData":[TD([[makeQuery(id+"F6.imprint","IMPRINT",EDGE,{"disambiguationData":[TD([[subQ3,-1.0]])],"derivedFrom":subQ0}),1.0]])]});}
            var Q1;
            {var subQ0=sQuery(id+"F6.wireOp",EDGE,"E19");var subQ1=sQuery(id+"F0.wireOp",EDGE,"E0.right");var subQ2=makeQuery(id+"F2.opFillet","BLEND_EDGE",EDGE,{"blendedFrom":[makeQuery(id+"F1.opExtrude","CAP_EDGE",EDGE,{"disambiguationData":[OSD([subQ1])],"isStart":false}),makeQuery(id+"F1.opExtrude","CAP_FACE",FACE,{"disambiguationData":[OSD([sQuery(id+"F0.wireOp",EDGE,"E0.bottom"),sQuery(id+"F0.wireOp",EDGE,"E0.top"),sQuery(id+"F0.wireOp",EDGE,"E0.left"),subQ1])],"isStart":false})],"blendedInto":[makeQuery(id+"F1.opExtrude","CAP_FACE",FACE,{"disambiguationData":[OSD([sQuery(id+"F0.wireOp",EDGE,"E0.bottom"),sQuery(id+"F0.wireOp",EDGE,"E0.top"),sQuery(id+"F0.wireOp",EDGE,"E0.left"),subQ1])],"isStart":false})]});var subQ3=makeQuery(id+"F6.imprint","INTERSECT",VERTEX,{"disambiguationData":[OD(0.0)],"derivedFrom":[subQ2,subQ0]});Q1=makeQuery(id+"F6.imprint","IMPRINT",FACE,{"disambiguationData":[TD([[makeQuery(id+"F6.imprint","IMPRINT",EDGE,{"disambiguationData":[TD([[subQ3,1.0]])],"derivedFrom":subQ0}),1.0]])]});}
            var Q2;
            {var subQ0=sQuery(id+"F6.wireOp",EDGE,"E20");var subQ1=sQuery(id+"F0.wireOp",EDGE,"E0.right");var subQ2=makeQuery(id+"F2.opFillet","BLEND_EDGE",EDGE,{"blendedFrom":[makeQuery(id+"F1.opExtrude","CAP_EDGE",EDGE,{"disambiguationData":[OSD([subQ1])],"isStart":false}),makeQuery(id+"F1.opExtrude","CAP_FACE",FACE,{"disambiguationData":[OSD([sQuery(id+"F0.wireOp",EDGE,"E0.bottom"),sQuery(id+"F0.wireOp",EDGE,"E0.top"),sQuery(id+"F0.wireOp",EDGE,"E0.left"),subQ1])],"isStart":false})],"blendedInto":[makeQuery(id+"F1.opExtrude","CAP_FACE",FACE,{"disambiguationData":[OSD([sQuery(id+"F0.wireOp",EDGE,"E0.bottom"),sQuery(id+"F0.wireOp",EDGE,"E0.top"),sQuery(id+"F0.wireOp",EDGE,"E0.left"),subQ1])],"isStart":false})]});var subQ3=makeQuery(id+"F6.imprint","INTERSECT",VERTEX,{"disambiguationData":[OD(0.0)],"derivedFrom":[subQ2,subQ0]});Q2=makeQuery(id+"F6.imprint","IMPRINT",FACE,{"disambiguationData":[TD([[makeQuery(id+"F6.imprint","IMPRINT",EDGE,{"disambiguationData":[TD([[subQ3,1.0]])],"derivedFrom":subQ0}),1.0]])]});}
            var Q3;
            {var subQ0=sQuery(id+"F6.wireOp",EDGE,"E22.MirrorC");var subQ1=sQuery(id+"F0.wireOp",EDGE,"E0.left");var subQ2=makeQuery(id+"F2.opFillet","BLEND_EDGE",EDGE,{"blendedFrom":[makeQuery(id+"F1.opExtrude","CAP_EDGE",EDGE,{"disambiguationData":[OSD([subQ1])],"isStart":false}),makeQuery(id+"F1.opExtrude","CAP_FACE",FACE,{"disambiguationData":[OSD([sQuery(id+"F0.wireOp",EDGE,"E0.bottom"),sQuery(id+"F0.wireOp",EDGE,"E0.top"),subQ1,sQuery(id+"F0.wireOp",EDGE,"E0.right")])],"isStart":false})],"blendedInto":[makeQuery(id+"F1.opExtrude","CAP_FACE",FACE,{"disambiguationData":[OSD([sQuery(id+"F0.wireOp",EDGE,"E0.bottom"),sQuery(id+"F0.wireOp",EDGE,"E0.top"),subQ1,sQuery(id+"F0.wireOp",EDGE,"E0.right")])],"isStart":false})]});var subQ3=makeQuery(id+"F6.imprint","INTERSECT",VERTEX,{"disambiguationData":[OD(0.0)],"derivedFrom":[subQ2,subQ0]});Q3=makeQuery(id+"F6.imprint","IMPRINT",FACE,{"disambiguationData":[TD([[makeQuery(id+"F6.imprint","IMPRINT",EDGE,{"disambiguationData":[TD([[subQ3,1.0]])],"derivedFrom":subQ0}),-1.0]])]});}
            var Q4;
            {var subQ0=sQuery(id+"F6.wireOp",EDGE,"E21.MirrorC");var subQ1=sQuery(id+"F0.wireOp",EDGE,"E0.left");var subQ2=makeQuery(id+"F2.opFillet","BLEND_EDGE",EDGE,{"blendedFrom":[makeQuery(id+"F1.opExtrude","CAP_EDGE",EDGE,{"disambiguationData":[OSD([subQ1])],"isStart":false}),makeQuery(id+"F1.opExtrude","CAP_FACE",FACE,{"disambiguationData":[OSD([sQuery(id+"F0.wireOp",EDGE,"E0.bottom"),sQuery(id+"F0.wireOp",EDGE,"E0.top"),subQ1,sQuery(id+"F0.wireOp",EDGE,"E0.right")])],"isStart":false})],"blendedInto":[makeQuery(id+"F1.opExtrude","CAP_FACE",FACE,{"disambiguationData":[OSD([sQuery(id+"F0.wireOp",EDGE,"E0.bottom"),sQuery(id+"F0.wireOp",EDGE,"E0.top"),subQ1,sQuery(id+"F0.wireOp",EDGE,"E0.right")])],"isStart":false})]});var subQ3=makeQuery(id+"F6.imprint","INTERSECT",VERTEX,{"disambiguationData":[OD(0.0)],"derivedFrom":[subQ2,subQ0]});Q4=makeQuery(id+"F6.imprint","IMPRINT",FACE,{"disambiguationData":[TD([[makeQuery(id+"F6.imprint","IMPRINT",EDGE,{"disambiguationData":[TD([[subQ3,-1.0]])],"derivedFrom":subQ0}),-1.0]])]});}
            var Q5;
            {var subQ0=sQuery(id+"F6.wireOp",EDGE,"E21.MirrorC");var subQ1=sQuery(id+"F0.wireOp",EDGE,"E0.left");var subQ2=makeQuery(id+"F2.opFillet","BLEND_EDGE",EDGE,{"blendedFrom":[makeQuery(id+"F1.opExtrude","CAP_EDGE",EDGE,{"disambiguationData":[OSD([subQ1])],"isStart":false}),makeQuery(id+"F1.opExtrude","CAP_FACE",FACE,{"disambiguationData":[OSD([sQuery(id+"F0.wireOp",EDGE,"E0.bottom"),sQuery(id+"F0.wireOp",EDGE,"E0.top"),subQ1,sQuery(id+"F0.wireOp",EDGE,"E0.right")])],"isStart":false})],"blendedInto":[makeQuery(id+"F1.opExtrude","CAP_FACE",FACE,{"disambiguationData":[OSD([sQuery(id+"F0.wireOp",EDGE,"E0.bottom"),sQuery(id+"F0.wireOp",EDGE,"E0.top"),subQ1,sQuery(id+"F0.wireOp",EDGE,"E0.right")])],"isStart":false})]});var subQ3=makeQuery(id+"F6.imprint","INTERSECT",VERTEX,{"disambiguationData":[OD(0.0)],"derivedFrom":[subQ2,subQ0]});Q5=makeQuery(id+"F6.imprint","IMPRINT",FACE,{"disambiguationData":[TD([[makeQuery(id+"F6.imprint","IMPRINT",EDGE,{"disambiguationData":[TD([[subQ3,1.0]])],"derivedFrom":subQ0}),-1.0]])]});}
            var Q6;
            {var subQ0=sQuery(id+"F6.wireOp",EDGE,"E22.MirrorC");var subQ1=sQuery(id+"F0.wireOp",EDGE,"E0.left");var subQ2=makeQuery(id+"F2.opFillet","BLEND_EDGE",EDGE,{"blendedFrom":[makeQuery(id+"F1.opExtrude","CAP_EDGE",EDGE,{"disambiguationData":[OSD([subQ1])],"isStart":false}),makeQuery(id+"F1.opExtrude","CAP_FACE",FACE,{"disambiguationData":[OSD([sQuery(id+"F0.wireOp",EDGE,"E0.bottom"),sQuery(id+"F0.wireOp",EDGE,"E0.top"),subQ1,sQuery(id+"F0.wireOp",EDGE,"E0.right")])],"isStart":false})],"blendedInto":[makeQuery(id+"F1.opExtrude","CAP_FACE",FACE,{"disambiguationData":[OSD([sQuery(id+"F0.wireOp",EDGE,"E0.bottom"),sQuery(id+"F0.wireOp",EDGE,"E0.top"),subQ1,sQuery(id+"F0.wireOp",EDGE,"E0.right")])],"isStart":false})]});var subQ3=makeQuery(id+"F6.imprint","INTERSECT",VERTEX,{"disambiguationData":[OD(0.0)],"derivedFrom":[subQ2,subQ0]});Q6=makeQuery(id+"F6.imprint","IMPRINT",FACE,{"disambiguationData":[TD([[makeQuery(id+"F6.imprint","IMPRINT",EDGE,{"disambiguationData":[TD([[subQ3,-1.0]])],"derivedFrom":subQ0}),-1.0]])]});}
            var Q7;
            {var subQ0=sQuery(id+"F6.wireOp",EDGE,"E20");var subQ1=sQuery(id+"F0.wireOp",EDGE,"E0.right");var subQ2=makeQuery(id+"F2.opFillet","BLEND_EDGE",EDGE,{"blendedFrom":[makeQuery(id+"F1.opExtrude","CAP_EDGE",EDGE,{"disambiguationData":[OSD([subQ1])],"isStart":false}),makeQuery(id+"F1.opExtrude","CAP_FACE",FACE,{"disambiguationData":[OSD([sQuery(id+"F0.wireOp",EDGE,"E0.bottom"),sQuery(id+"F0.wireOp",EDGE,"E0.top"),sQuery(id+"F0.wireOp",EDGE,"E0.left"),subQ1])],"isStart":false})],"blendedInto":[makeQuery(id+"F1.opExtrude","CAP_FACE",FACE,{"disambiguationData":[OSD([sQuery(id+"F0.wireOp",EDGE,"E0.bottom"),sQuery(id+"F0.wireOp",EDGE,"E0.top"),sQuery(id+"F0.wireOp",EDGE,"E0.left"),subQ1])],"isStart":false})]});var subQ3=makeQuery(id+"F6.imprint","INTERSECT",VERTEX,{"disambiguationData":[OD(0.0)],"derivedFrom":[subQ2,subQ0]});Q7=makeQuery(id+"F6.imprint","IMPRINT",FACE,{"disambiguationData":[TD([[makeQuery(id+"F6.imprint","IMPRINT",EDGE,{"disambiguationData":[TD([[subQ3,-1.0]])],"derivedFrom":subQ0}),1.0]])]});}
            var Q8;
            Q8=sQuery(id+"F6.wireOp",EDGE,"E19");
            var Q9;
            Q9=sQuery(id+"F6.wireOp",EDGE,"E21.MirrorC");
            var Q10;
            Q10=sQuery(id+"F6.wireOp",EDGE,"E22.MirrorC");
            var Q11;
            Q11=sQuery(id+"F6.wireOp",EDGE,"E20");
            extrude(context, id + "F11", {"entities" : qUnion([Q0, Q1, Q2, Q3, Q4, Q5, Q6, Q7]), "operationType" : NewBodyOperationType.REMOVE, "surfaceEntities" : qUnion([Q8, Q9, Q10, Q11]), "endBound" : BoundingType.THROUGH_ALL, "oppositeDirection" : true, "depth" : 25 * mm});
        }
        {
            var Q0;
            Q0=qCreatedBy(makeId("Front.planeOp"),FACE);
            cPlane(context, id + "F12", {"entities" : qUnion([Q0]), "cplaneType" : CPlaneType.OFFSET, "offset" : 50 * mm, "width" : 150 * mm, "height" : 150 * mm});
        }
        {
            var Q0;
            Q0=qCreatedBy(id+"F12.planeOp",FACE);
            var sketch = newSketch(context, id + "F13", { "sketchPlane" : qUnion([Q0])});
            skLineSegment(sketch, "E23", {"start": v(0, 0) * mm, "end": v(0, 52) * mm, "construction": true});
            skLineSegment(sketch, "E24", {"start": v(-78, 0) * mm, "end": v(-75.34, 27.59) * mm});
            skPoint(sketch, "E25.visualSharp", {"position": v(-73, 52) * mm});
            skArc(sketch, "E25.filletArc", {"start": v(-59.22, 49.77) * mm, "mid": v(-70.3, 40.88) * mm, "end": v(-75.34, 27.59) * mm});
            skPoint(sketch, "E26", {"position": v(-36.4, 49.77) * mm});
            skLineSegment(sketch, "E27", {"start": v(-59.22, 49.77) * mm, "end": v(0, 49.77) * mm});
            skLineSegment(sketch, "E28", {"start": v(-33.5, 49.77) * mm, "end": v(-23.5, 59.77) * mm});
            skLineSegment(sketch, "E29", {"start": v(-23.5, 59.77) * mm, "end": v(0, 59.77) * mm});
            skLineSegment(sketch, "E30", {"start": v(-78, 0) * mm, "end": v(0, 0) * mm});
            skLineSegment(sketch, "E31.MirrorCS", {"start": v(23.5, 59.77) * mm, "end": v(0, 59.77) * mm});
            skLineSegment(sketch, "E32.MirrorCS", {"start": v(33.5, 49.77) * mm, "end": v(23.5, 59.77) * mm});
            skLineSegment(sketch, "E33.MirrorCS", {"start": v(59.22, 49.77) * mm, "end": v(0, 49.77) * mm});
            skArc(sketch, "E34.MirrorCS", {"start": v(59.22, 49.77) * mm, "mid": v(70.3, 40.88) * mm, "end": v(75.34, 27.59) * mm});
            skLineSegment(sketch, "E35.MirrorCS", {"start": v(78, 0) * mm, "end": v(75.34, 27.59) * mm});
            skLineSegment(sketch, "E36.MirrorCS", {"start": v(78, 0) * mm, "end": v(0, 0) * mm});
            skSolve(sketch);
        }
        {
            var Q0;
            Q0=makeQuery(id+"F13.imprint","IMPRINT",FACE,{"disambiguationData":[TD([[makeQuery(id+"F13.imprint","IMPRINT",EDGE,{"derivedFrom":sQuery(id+"F13.wireOp",EDGE,"E24")}),-1.0]])]});
            extrude(context, id + "F14", {"entities" : qUnion([Q0]), "operationType" : NewBodyOperationType.REMOVE, "oppositeDirection" : true, "depth" : 25 * mm});
        }
        {
            var Q0;
            {var subQ0=sQuery(id+"F13.wireOp",EDGE,"E28");Q0=makeQuery(id+"F13.imprint","IMPRINT",FACE,{"disambiguationData":[TD([[makeQuery(id+"F13.imprint","IMPRINT",EDGE,{"derivedFrom":subQ0}),-1.0]])]});}
            var Q1;
            Q1=makeQuery(id+"F10.boolean.opBoolean","SPLIT",BODY,{"disambiguationData":[OD(0.0)],"derivedFrom":makeQuery(id+"F1.opExtrude","SWEPT_BODY",BODY,{"disambiguationData":[OSD([sQuery(id+"F0.wireOp",EDGE,"E0.bottom"),sQuery(id+"F0.wireOp",EDGE,"E0.top"),sQuery(id+"F0.wireOp",EDGE,"E0.left"),sQuery(id+"F0.wireOp",EDGE,"E0.right")])]})});
            extrude(context, id + "F15", {"entities" : qUnion([Q0]), "operationType" : NewBodyOperationType.REMOVE, "oppositeDirection" : true, "endBoundEntityBody" : qUnion([Q1]), "depth" : 12 * mm});
        }
    });
